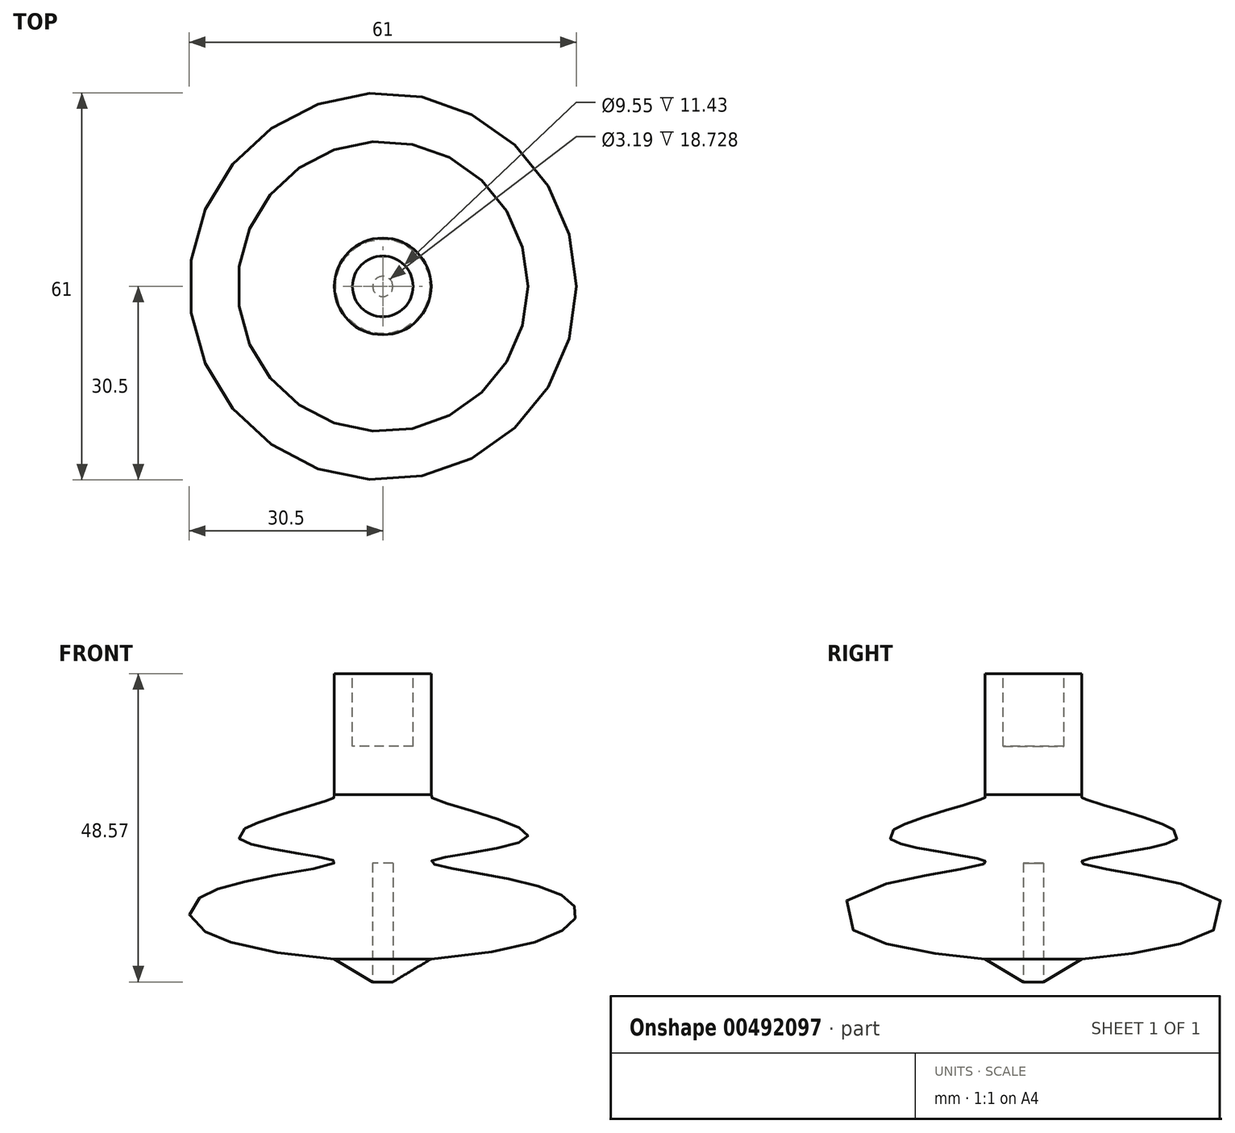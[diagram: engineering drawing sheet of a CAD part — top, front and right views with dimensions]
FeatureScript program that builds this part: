
annotation { "Feature Type Name" : "Feature", "Feature Type Description" : "" }
export const myFeature = defineFeature(function(context is Context, id is Id, definition is map)
    precondition{}
    {
        {
            var Q0;
            Q0=qCreatedBy(makeId("Front.planeOp"),FACE);
            var sketch = newSketch(context, id + "F0", { "sketchPlane" : qUnion([Q0])});
            skLineSegment(sketch, "E0", {"start": v(0, 0) * mm, "end": v(7.62, 4.58) * mm});
            skFitSpline(sketch, "E1", {"points": [v(7.62, 4.58) * mm, v(27.94, 14.75) * mm, v(7.62, 19.97) * mm, v(22.86, 23.93) * mm, v(7.62, 30) * mm, v(7.62, 30.48) * mm], "startDerivative": vector(251.56, 19.17) * mm, "endDerivative": vector(12.82, 14.28) * mm});
            skLineSegment(sketch, "E2", {"start": v(7.62, 30.48) * mm, "end": v(7.62, 49.53) * mm});
            skLineSegment(sketch, "E3", {"start": v(7.62, 49.53) * mm, "end": v(0, 49.53) * mm});
            skLineSegment(sketch, "E4", {"start": v(0, 49.53) * mm, "end": v(0, 0) * mm});
            skSolve(sketch);
        }
        {
            var Q0;
            Q0=makeQuery(id+"F0.imprint","IMPRINT",FACE,{"disambiguationData":[TD([[makeQuery(id+"F0.imprint","IMPRINT",EDGE,{"derivedFrom":sQuery(id+"F0.wireOp",EDGE,"E0")}),1.0]])]});
            var Q1;
            Q1=sQuery(id+"F0.wireOp",EDGE,"E4");
            revolve(context, id + "F1", {"entities" : qUnion([Q0]), "axis" : qUnion([Q1]), "revolveType" : RevolveType.FULL});
        }
        {
            var Q0;
            Q0=makeQuery(id+"F1.opRevolve","SWEPT_FACE",FACE,{"disambiguationData":[OSD([sQuery(id+"F0.wireOp",EDGE,"E3")])]});
            var sketch = newSketch(context, id + "F2", { "sketchPlane" : qUnion([Q0])});
            skCircle(sketch, "E5", {"center": v(0, 0) * mm, "radius": 4.78 * mm});
            skSolve(sketch);
        }
        {
            var Q0;
            Q0=makeQuery(id+"F2.imprint","IMPRINT",FACE,{"disambiguationData":[TD([[makeQuery(id+"F2.imprint","IMPRINT",EDGE,{"derivedFrom":sQuery(id+"F2.wireOp",EDGE,"E5")}),1.0]])]});
            var Q1;
            Q1=sQuery(id+"F2.wireOp",EDGE,"E5");
            extrude(context, id + "F3", {"entities" : qUnion([Q0]), "operationType" : NewBodyOperationType.REMOVE, "surfaceEntities" : qUnion([Q1]), "oppositeDirection" : true, "depth" : 11.43 * mm});
        }
        {
            var Q0;
            Q0=qCreatedBy(makeId("Top.planeOp"),FACE);
            var sketch = newSketch(context, id + "F4", { "sketchPlane" : qUnion([Q0])});
            skCircle(sketch, "E6", {"center": v(0, 0) * mm, "radius": 1.6 * mm});
            skSolve(sketch);
        }
        {
            var Q0;
            Q0=makeQuery(id+"F4.imprint","IMPRINT",FACE,{"disambiguationData":[TD([[makeQuery(id+"F4.imprint","IMPRINT",EDGE,{"derivedFrom":sQuery(id+"F4.wireOp",EDGE,"E6")}),1.0]])]});
            extrude(context, id + "F5", {"entities" : qUnion([Q0]), "operationType" : NewBodyOperationType.REMOVE, "depth" : 19.68 * mm});
        }
    });
